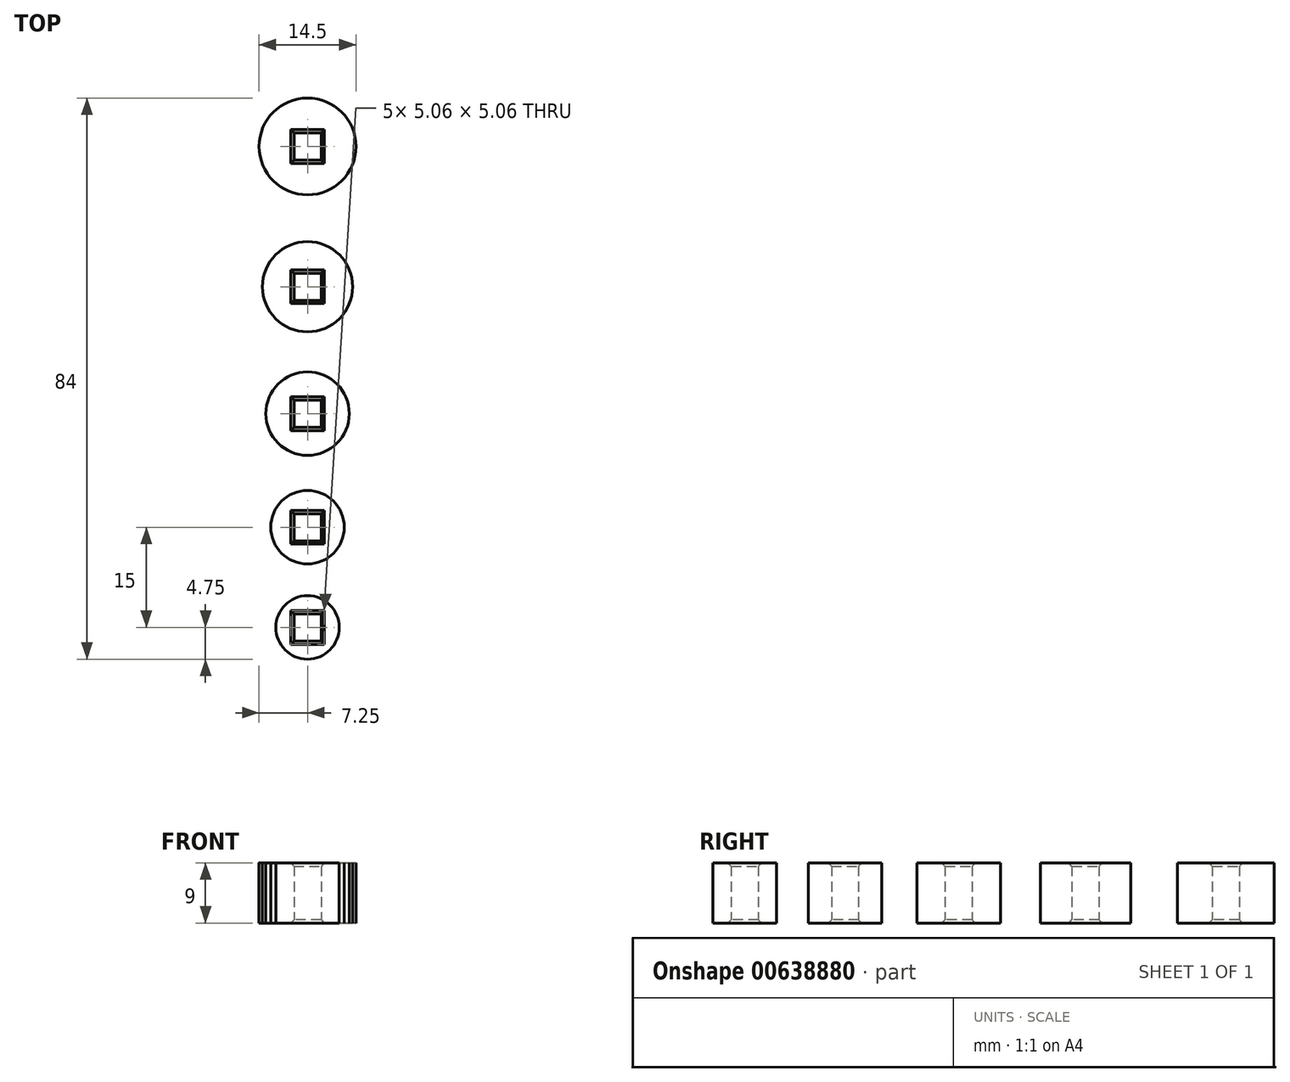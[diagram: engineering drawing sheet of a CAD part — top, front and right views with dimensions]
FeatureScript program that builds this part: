
annotation { "Feature Type Name" : "Feature", "Feature Type Description" : "" }
export const myFeature = defineFeature(function(context is Context, id is Id, definition is map)
    precondition{}
    {
        {
            var Q0;
            Q0=qCreatedBy(makeId("Top.planeOp"),FACE);
            var sketch = newSketch(context, id + "F0", { "sketchPlane" : qUnion([Q0])});
            skLineSegment(sketch, "E0", {"start": v(0, 0) * mm, "end": v(0, 19) * mm, "construction": true});
            skLineSegment(sketch, "E1", {"start": v(0, 19) * mm, "end": v(0, 40) * mm, "construction": true});
            skLineSegment(sketch, "E2", {"start": v(0, 0) * mm, "end": v(0, -17) * mm, "construction": true});
            skLineSegment(sketch, "E3", {"start": v(0, -17) * mm, "end": v(0, -32) * mm, "construction": true});
            skCircle(sketch, "E4", {"center": v(0, 40) * mm, "radius": 7.25 * mm});
            skCircle(sketch, "E5", {"center": v(0, 19) * mm, "radius": 6.75 * mm});
            skCircle(sketch, "E6", {"center": v(0, 0) * mm, "radius": 6.25 * mm});
            skCircle(sketch, "E7", {"center": v(0, -17) * mm, "radius": 5.5 * mm});
            skCircle(sketch, "E8", {"center": v(0, -32) * mm, "radius": 4.75 * mm});
            skLineSegment(sketch, "E9.bottom", {"start": v(2.03, 37.97) * mm, "end": v(-2.03, 37.97) * mm});
            skLineSegment(sketch, "E9.top", {"start": v(2.03, 42.03) * mm, "end": v(-2.03, 42.03) * mm});
            skLineSegment(sketch, "E9.left", {"start": v(2.03, 37.97) * mm, "end": v(2.03, 42.03) * mm});
            skLineSegment(sketch, "E9.right", {"start": v(-2.03, 37.97) * mm, "end": v(-2.03, 42.03) * mm});
            skLineSegment(sketch, "E10.bottom", {"start": v(2.03, 16.97) * mm, "end": v(-2.03, 16.97) * mm});
            skLineSegment(sketch, "E10.top", {"start": v(2.03, 21.03) * mm, "end": v(-2.03, 21.03) * mm});
            skLineSegment(sketch, "E10.left", {"start": v(2.03, 16.97) * mm, "end": v(2.03, 21.03) * mm});
            skLineSegment(sketch, "E10.right", {"start": v(-2.03, 16.97) * mm, "end": v(-2.03, 21.03) * mm});
            skLineSegment(sketch, "E11.bottom", {"start": v(2.03, -2.03) * mm, "end": v(-2.03, -2.03) * mm});
            skLineSegment(sketch, "E11.top", {"start": v(2.03, 2.03) * mm, "end": v(-2.03, 2.03) * mm});
            skLineSegment(sketch, "E11.left", {"start": v(2.03, -2.03) * mm, "end": v(2.03, 2.03) * mm});
            skLineSegment(sketch, "E11.right", {"start": v(-2.03, -2.03) * mm, "end": v(-2.03, 2.03) * mm});
            skLineSegment(sketch, "E12.bottom", {"start": v(2.03, -19.03) * mm, "end": v(-2.03, -19.03) * mm});
            skLineSegment(sketch, "E12.top", {"start": v(2.03, -14.97) * mm, "end": v(-2.03, -14.97) * mm});
            skLineSegment(sketch, "E12.left", {"start": v(2.03, -19.03) * mm, "end": v(2.03, -14.97) * mm});
            skLineSegment(sketch, "E12.right", {"start": v(-2.03, -19.03) * mm, "end": v(-2.03, -14.97) * mm});
            skLineSegment(sketch, "E13.bottom", {"start": v(2.03, -34.03) * mm, "end": v(-2.03, -34.03) * mm});
            skLineSegment(sketch, "E13.top", {"start": v(2.03, -29.97) * mm, "end": v(-2.03, -29.97) * mm});
            skLineSegment(sketch, "E13.left", {"start": v(2.03, -34.03) * mm, "end": v(2.03, -29.97) * mm});
            skLineSegment(sketch, "E13.right", {"start": v(-2.03, -34.03) * mm, "end": v(-2.03, -29.97) * mm});
            skSolve(sketch);
        }
        {
            var Q0;
            Q0=makeQuery(id+"F0.imprint","IMPRINT",FACE,{"disambiguationData":[TD([[makeQuery(id+"F0.imprint","IMPRINT",EDGE,{"derivedFrom":sQuery(id+"F0.wireOp",EDGE,"E8")}),1.0]])]});
            var Q1;
            Q1=makeQuery(id+"F0.imprint","IMPRINT",FACE,{"disambiguationData":[TD([[makeQuery(id+"F0.imprint","IMPRINT",EDGE,{"derivedFrom":sQuery(id+"F0.wireOp",EDGE,"E7")}),1.0]])]});
            var Q2;
            Q2=makeQuery(id+"F0.imprint","IMPRINT",FACE,{"disambiguationData":[TD([[makeQuery(id+"F0.imprint","IMPRINT",EDGE,{"derivedFrom":sQuery(id+"F0.wireOp",EDGE,"E6")}),1.0]])]});
            var Q3;
            Q3=makeQuery(id+"F0.imprint","IMPRINT",FACE,{"disambiguationData":[TD([[makeQuery(id+"F0.imprint","IMPRINT",EDGE,{"derivedFrom":sQuery(id+"F0.wireOp",EDGE,"E5")}),1.0]])]});
            var Q4;
            Q4=makeQuery(id+"F0.imprint","IMPRINT",FACE,{"disambiguationData":[TD([[makeQuery(id+"F0.imprint","IMPRINT",EDGE,{"derivedFrom":sQuery(id+"F0.wireOp",EDGE,"E4")}),1.0]])]});
            extrude(context, id + "F1", {"entities" : qUnion([Q0, Q1, Q2, Q3, Q4]), "depth" : 9 * mm, "offsetDistance" : 25 * mm});
        }
        {
            var Q0;
            Q0=makeQuery(id+"F1.opExtrude","CAP_EDGE",EDGE,{"disambiguationData":[OSD([sQuery(id+"F0.wireOp",EDGE,"E9.top")])],"isStart":false});
            var Q1;
            Q1=makeQuery(id+"F1.opExtrude","CAP_EDGE",EDGE,{"disambiguationData":[OSD([sQuery(id+"F0.wireOp",EDGE,"E9.right")])],"isStart":false});
            var Q2;
            Q2=makeQuery(id+"F1.opExtrude","CAP_EDGE",EDGE,{"disambiguationData":[OSD([sQuery(id+"F0.wireOp",EDGE,"E9.bottom")])],"isStart":false});
            var Q3;
            Q3=makeQuery(id+"F1.opExtrude","CAP_EDGE",EDGE,{"disambiguationData":[OSD([sQuery(id+"F0.wireOp",EDGE,"E9.left")])],"isStart":false});
            var Q4;
            Q4=makeQuery(id+"F1.opExtrude","CAP_EDGE",EDGE,{"disambiguationData":[OSD([sQuery(id+"F0.wireOp",EDGE,"E10.right")])],"isStart":false});
            var Q5;
            Q5=makeQuery(id+"F1.opExtrude","CAP_EDGE",EDGE,{"disambiguationData":[OSD([sQuery(id+"F0.wireOp",EDGE,"E10.top")])],"isStart":false});
            var Q6;
            Q6=makeQuery(id+"F1.opExtrude","CAP_EDGE",EDGE,{"disambiguationData":[OSD([sQuery(id+"F0.wireOp",EDGE,"E10.left")])],"isStart":false});
            var Q7;
            Q7=makeQuery(id+"F1.opExtrude","CAP_EDGE",EDGE,{"disambiguationData":[OSD([sQuery(id+"F0.wireOp",EDGE,"E10.bottom")])],"isStart":false});
            var Q8;
            Q8=makeQuery(id+"F1.opExtrude","CAP_EDGE",EDGE,{"disambiguationData":[OSD([sQuery(id+"F0.wireOp",EDGE,"E11.right")])],"isStart":false});
            var Q9;
            Q9=makeQuery(id+"F1.opExtrude","CAP_EDGE",EDGE,{"disambiguationData":[OSD([sQuery(id+"F0.wireOp",EDGE,"E11.top")])],"isStart":false});
            var Q10;
            Q10=makeQuery(id+"F1.opExtrude","CAP_EDGE",EDGE,{"disambiguationData":[OSD([sQuery(id+"F0.wireOp",EDGE,"E11.bottom")])],"isStart":false});
            var Q11;
            Q11=makeQuery(id+"F1.opExtrude","CAP_EDGE",EDGE,{"disambiguationData":[OSD([sQuery(id+"F0.wireOp",EDGE,"E11.left")])],"isStart":false});
            var Q12;
            Q12=makeQuery(id+"F1.opExtrude","CAP_EDGE",EDGE,{"disambiguationData":[OSD([sQuery(id+"F0.wireOp",EDGE,"E12.right")])],"isStart":false});
            var Q13;
            Q13=makeQuery(id+"F1.opExtrude","CAP_EDGE",EDGE,{"disambiguationData":[OSD([sQuery(id+"F0.wireOp",EDGE,"E12.top")])],"isStart":false});
            var Q14;
            Q14=makeQuery(id+"F1.opExtrude","CAP_EDGE",EDGE,{"disambiguationData":[OSD([sQuery(id+"F0.wireOp",EDGE,"E12.left")])],"isStart":false});
            var Q15;
            Q15=makeQuery(id+"F1.opExtrude","CAP_EDGE",EDGE,{"disambiguationData":[OSD([sQuery(id+"F0.wireOp",EDGE,"E12.bottom")])],"isStart":false});
            var Q16;
            Q16=makeQuery(id+"F1.opExtrude","CAP_EDGE",EDGE,{"disambiguationData":[OSD([sQuery(id+"F0.wireOp",EDGE,"E13.right")])],"isStart":false});
            var Q17;
            Q17=makeQuery(id+"F1.opExtrude","CAP_EDGE",EDGE,{"disambiguationData":[OSD([sQuery(id+"F0.wireOp",EDGE,"E13.top")])],"isStart":false});
            var Q18;
            Q18=makeQuery(id+"F1.opExtrude","CAP_EDGE",EDGE,{"disambiguationData":[OSD([sQuery(id+"F0.wireOp",EDGE,"E13.left")])],"isStart":false});
            var Q19;
            Q19=makeQuery(id+"F1.opExtrude","CAP_EDGE",EDGE,{"disambiguationData":[OSD([sQuery(id+"F0.wireOp",EDGE,"E13.bottom")])],"isStart":false});
            chamfer(context, id + "F2", {"entities" : qUnion([Q0, Q1, Q2, Q3, Q4, Q5, Q6, Q7, Q8, Q9, Q10, Q11, Q12, Q13, Q14, Q15, Q16, Q17, Q18, Q19]), "width" : .5 * mm, "tangentPropagation" : true});
        }
        {
            var Q0;
            Q0=makeQuery(id+"F1.opExtrude","CAP_EDGE",EDGE,{"disambiguationData":[OSD([sQuery(id+"F0.wireOp",EDGE,"E9.right")])],"isStart":true});
            var Q1;
            Q1=makeQuery(id+"F1.opExtrude","CAP_EDGE",EDGE,{"disambiguationData":[OSD([sQuery(id+"F0.wireOp",EDGE,"E9.bottom")])],"isStart":true});
            var Q2;
            Q2=makeQuery(id+"F1.opExtrude","CAP_EDGE",EDGE,{"disambiguationData":[OSD([sQuery(id+"F0.wireOp",EDGE,"E9.top")])],"isStart":true});
            var Q3;
            Q3=makeQuery(id+"F1.opExtrude","CAP_EDGE",EDGE,{"disambiguationData":[OSD([sQuery(id+"F0.wireOp",EDGE,"E9.left")])],"isStart":true});
            var Q4;
            Q4=makeQuery(id+"F1.opExtrude","CAP_EDGE",EDGE,{"disambiguationData":[OSD([sQuery(id+"F0.wireOp",EDGE,"E10.right")])],"isStart":true});
            var Q5;
            Q5=makeQuery(id+"F1.opExtrude","CAP_EDGE",EDGE,{"disambiguationData":[OSD([sQuery(id+"F0.wireOp",EDGE,"E10.bottom")])],"isStart":true});
            var Q6;
            Q6=makeQuery(id+"F1.opExtrude","CAP_EDGE",EDGE,{"disambiguationData":[OSD([sQuery(id+"F0.wireOp",EDGE,"E10.left")])],"isStart":true});
            var Q7;
            Q7=makeQuery(id+"F1.opExtrude","CAP_EDGE",EDGE,{"disambiguationData":[OSD([sQuery(id+"F0.wireOp",EDGE,"E10.top")])],"isStart":true});
            var Q8;
            Q8=makeQuery(id+"F1.opExtrude","CAP_EDGE",EDGE,{"disambiguationData":[OSD([sQuery(id+"F0.wireOp",EDGE,"E11.right")])],"isStart":true});
            var Q9;
            Q9=makeQuery(id+"F1.opExtrude","CAP_EDGE",EDGE,{"disambiguationData":[OSD([sQuery(id+"F0.wireOp",EDGE,"E11.top")])],"isStart":true});
            var Q10;
            Q10=makeQuery(id+"F1.opExtrude","CAP_EDGE",EDGE,{"disambiguationData":[OSD([sQuery(id+"F0.wireOp",EDGE,"E11.bottom")])],"isStart":true});
            var Q11;
            Q11=makeQuery(id+"F1.opExtrude","CAP_EDGE",EDGE,{"disambiguationData":[OSD([sQuery(id+"F0.wireOp",EDGE,"E11.left")])],"isStart":true});
            var Q12;
            Q12=makeQuery(id+"F1.opExtrude","CAP_EDGE",EDGE,{"disambiguationData":[OSD([sQuery(id+"F0.wireOp",EDGE,"E12.right")])],"isStart":true});
            var Q13;
            Q13=makeQuery(id+"F1.opExtrude","CAP_EDGE",EDGE,{"disambiguationData":[OSD([sQuery(id+"F0.wireOp",EDGE,"E12.bottom")])],"isStart":true});
            var Q14;
            Q14=makeQuery(id+"F1.opExtrude","CAP_EDGE",EDGE,{"disambiguationData":[OSD([sQuery(id+"F0.wireOp",EDGE,"E12.top")])],"isStart":true});
            var Q15;
            Q15=makeQuery(id+"F1.opExtrude","CAP_EDGE",EDGE,{"disambiguationData":[OSD([sQuery(id+"F0.wireOp",EDGE,"E12.left")])],"isStart":true});
            var Q16;
            Q16=makeQuery(id+"F1.opExtrude","CAP_EDGE",EDGE,{"disambiguationData":[OSD([sQuery(id+"F0.wireOp",EDGE,"E13.right")])],"isStart":true});
            var Q17;
            Q17=makeQuery(id+"F1.opExtrude","CAP_EDGE",EDGE,{"disambiguationData":[OSD([sQuery(id+"F0.wireOp",EDGE,"E13.bottom")])],"isStart":true});
            var Q18;
            Q18=makeQuery(id+"F1.opExtrude","CAP_EDGE",EDGE,{"disambiguationData":[OSD([sQuery(id+"F0.wireOp",EDGE,"E13.top")])],"isStart":true});
            var Q19;
            Q19=makeQuery(id+"F1.opExtrude","CAP_EDGE",EDGE,{"disambiguationData":[OSD([sQuery(id+"F0.wireOp",EDGE,"E13.left")])],"isStart":true});
            chamfer(context, id + "F3", {"entities" : qUnion([Q0, Q1, Q2, Q3, Q4, Q5, Q6, Q7, Q8, Q9, Q10, Q11, Q12, Q13, Q14, Q15, Q16, Q17, Q18, Q19]), "width" : .5 * mm, "tangentPropagation" : true});
        }
    });
